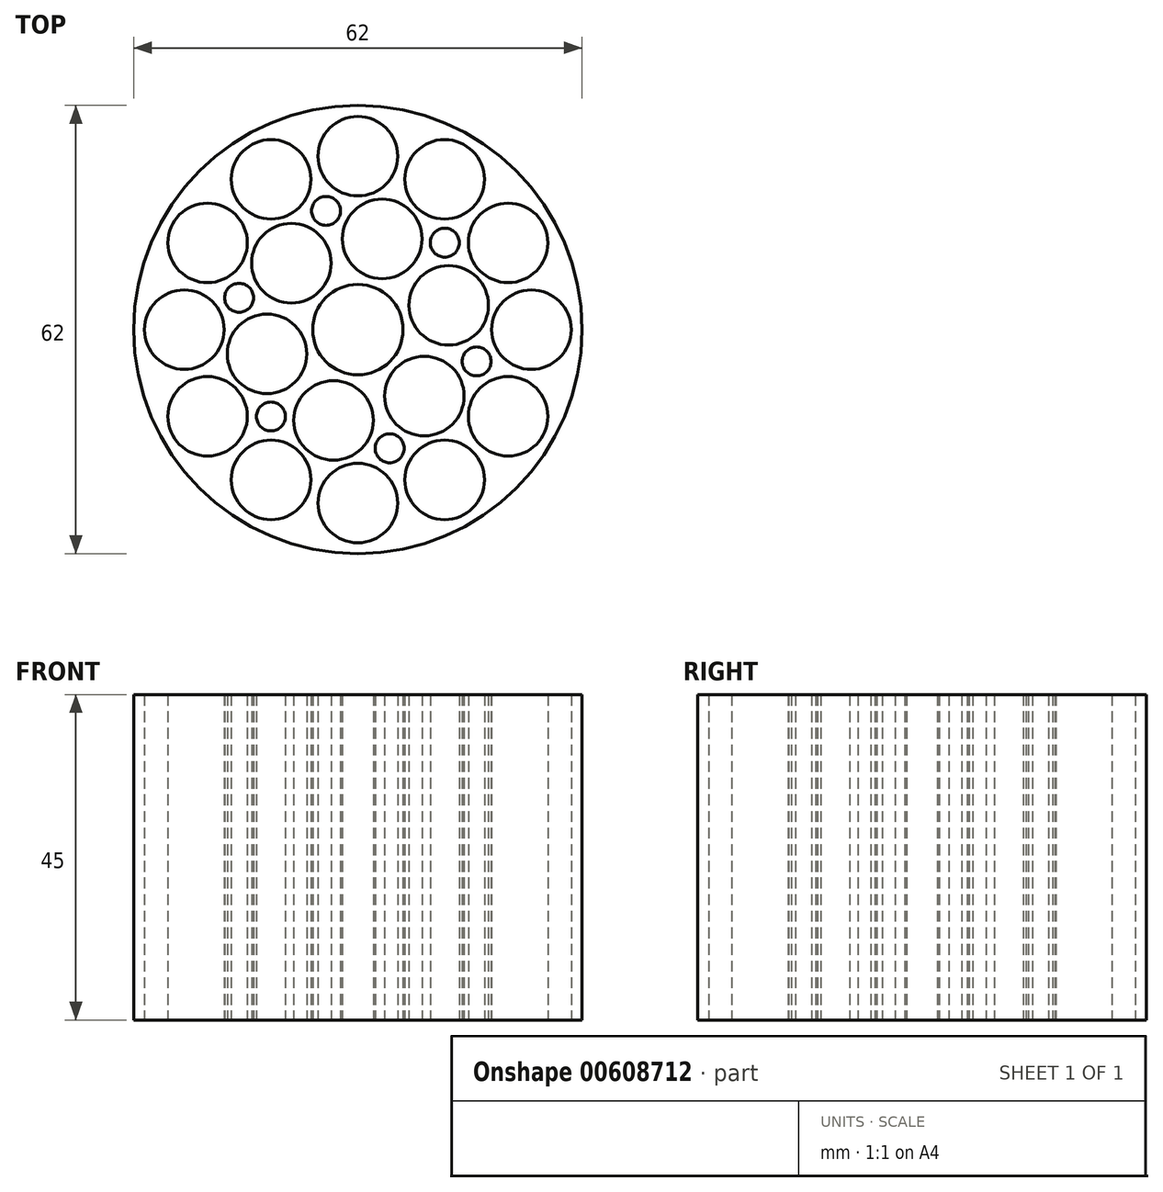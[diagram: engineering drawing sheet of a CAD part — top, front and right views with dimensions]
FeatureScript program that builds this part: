
annotation { "Feature Type Name" : "Feature", "Feature Type Description" : "" }
export const myFeature = defineFeature(function(context is Context, id is Id, definition is map)
    precondition{}
    {
        {
            var Q0;
            Q0=qCreatedBy(makeId("Top.planeOp"),FACE);
            var sketch = newSketch(context, id + "F0", { "sketchPlane" : qUnion([Q0])});
            skCircle(sketch, "E0", {"center": v(0, 0) * mm, "radius": 31 * mm});
            skSolve(sketch);
        }
        {
            var Q0;
            Q0=makeQuery(id+"F0.imprint","IMPRINT",FACE,{"disambiguationData":[TD([[makeQuery(id+"F0.imprint","IMPRINT",EDGE,{"derivedFrom":sQuery(id+"F0.wireOp",EDGE,"E0")}),1.0]])]});
            extrude(context, id + "F1", {"entities" : qUnion([Q0]), "depth" : 45 * mm, "offsetDistance" : 25 * mm});
        }
        {
            var Q0;
            Q0=makeQuery(id+"F1.opExtrude","CAP_FACE",FACE,{"disambiguationData":[OSD([sQuery(id+"F0.wireOp",EDGE,"E0")])],"isStart":true});
            var sketch = newSketch(context, id + "F2", { "sketchPlane" : qUnion([Q0])});
            skCircle(sketch, "E1", {"center": v(0, 0) * mm, "radius": 6.25 * mm});
            skSolve(sketch);
        }
        {
            var Q0;
            Q0 = qSketchRegion(id + "F2", true);
            extrude(context, id + "F3", {"entities" : qUnion([Q0]), "operationType" : NewBodyOperationType.REMOVE, "oppositeDirection" : true, "depth" : 51 * mm, "offsetDistance" : 25 * mm});
        }
        {
            var Q0;
            Q0=makeQuery(id+"F1.opExtrude","CAP_FACE",FACE,{"disambiguationData":[OSD([sQuery(id+"F0.wireOp",EDGE,"E0")])],"isStart":true});
            var sketch = newSketch(context, id + "F4", { "sketchPlane" : qUnion([Q0])});
            skCircle(sketch, "E2", {"center": v(0, 24) * mm, "radius": 5.5 * mm});
            skCircle(sketch, "E3.1.0", {"center": v(-12, 20.78) * mm, "radius": 5.5 * mm});
            skCircle(sketch, "E3.2.0", {"center": v(-20.78, 12) * mm, "radius": 5.5 * mm});
            skCircle(sketch, "E3.3.0", {"center": v(-24, 0) * mm, "radius": 5.5 * mm});
            skCircle(sketch, "E3.4.0", {"center": v(-20.78, -12) * mm, "radius": 5.5 * mm});
            skCircle(sketch, "E3.5.0", {"center": v(-12, -20.78) * mm, "radius": 5.5 * mm});
            skPoint(sketch, "E3.center", {"position": v(0, 0) * mm});
            skCircle(sketch, "E4.1.6.0", {"center": v(0, -24) * mm, "radius": 5.5 * mm});
            skCircle(sketch, "E4.1.7.0", {"center": v(12, -20.78) * mm, "radius": 5.5 * mm});
            skCircle(sketch, "E4.1.8.0", {"center": v(20.78, -12) * mm, "radius": 5.5 * mm});
            skCircle(sketch, "E4.1.9.0", {"center": v(24, 0) * mm, "radius": 5.5 * mm});
            skCircle(sketch, "E4.1.10.0", {"center": v(20.78, 12) * mm, "radius": 5.5 * mm});
            skCircle(sketch, "E4.1.11.0", {"center": v(12, 20.78) * mm, "radius": 5.5 * mm});
            skSolve(sketch);
        }
        {
            var Q0;
            Q0 = qSketchRegion(id + "F4", true);
            extrude(context, id + "F5", {"entities" : qUnion([Q0]), "operationType" : NewBodyOperationType.REMOVE, "oppositeDirection" : true, "depth" : 45 * mm, "offsetDistance" : 25 * mm});
        }
        {
            var Q0;
            Q0=makeQuery(id+"F1.opExtrude","CAP_FACE",FACE,{"disambiguationData":[OSD([sQuery(id+"F0.wireOp",EDGE,"E0")])],"isStart":true});
            var sketch = newSketch(context, id + "F6", { "sketchPlane" : qUnion([Q0])});
            skCircle(sketch, "E5", {"center": v(-12.56, 3.36) * mm, "radius": 5.5 * mm});
            skCircle(sketch, "E6.1.0", {"center": v(-9.2, -9.2) * mm, "radius": 5.5 * mm});
            skCircle(sketch, "E6.2.0", {"center": v(3.36, -12.56) * mm, "radius": 5.5 * mm});
            skCircle(sketch, "E6.3.0", {"center": v(12.56, -3.36) * mm, "radius": 5.5 * mm});
            skCircle(sketch, "E6.4.0", {"center": v(9.2, 9.2) * mm, "radius": 5.5 * mm});
            skCircle(sketch, "E6.5.0", {"center": v(-3.36, 12.56) * mm, "radius": 5.5 * mm});
            skPoint(sketch, "E6.center", {"position": v(0, 0) * mm});
            skSolve(sketch);
        }
        {
            var Q0;
            Q0 = qSketchRegion(id + "F2", true);
            var Q1;
            Q1 = qSketchRegion(id + "F6", true);
            extrude(context, id + "F7", {"entities" : qUnion([Q0, Q1]), "operationType" : NewBodyOperationType.REMOVE, "oppositeDirection" : true, "depth" : 45 * mm, "offsetDistance" : 25 * mm});
        }
        {
            var Q0;
            Q0=makeQuery(id+"F1.opExtrude","CAP_FACE",FACE,{"disambiguationData":[OSD([sQuery(id+"F0.wireOp",EDGE,"E0")])],"isStart":true});
            var sketch = newSketch(context, id + "F8", { "sketchPlane" : qUnion([Q0])});
            skCircle(sketch, "E7", {"center": v(4.4, 16.42) * mm, "radius": 2 * mm});
            skCircle(sketch, "E8.1.0", {"center": v(-12.02, 12.02) * mm, "radius": 2 * mm});
            skCircle(sketch, "E8.2.0", {"center": v(-16.42, -4.4) * mm, "radius": 2 * mm});
            skPoint(sketch, "E8.center", {"position": v(0, 0) * mm});
            skCircle(sketch, "E9.1.3.0", {"center": v(-4.4, -16.42) * mm, "radius": 2 * mm});
            skCircle(sketch, "E9.1.4.0", {"center": v(12.02, -12.02) * mm, "radius": 2 * mm});
            skCircle(sketch, "E9.1.5.0", {"center": v(16.42, 4.4) * mm, "radius": 2 * mm});
            skSolve(sketch);
        }
        {
            var Q0;
            Q0 = qSketchRegion(id + "F8", true);
            extrude(context, id + "F9", {"entities" : qUnion([Q0]), "operationType" : NewBodyOperationType.REMOVE, "oppositeDirection" : true, "depth" : 45 * mm, "offsetDistance" : 25 * mm});
        }
    });
